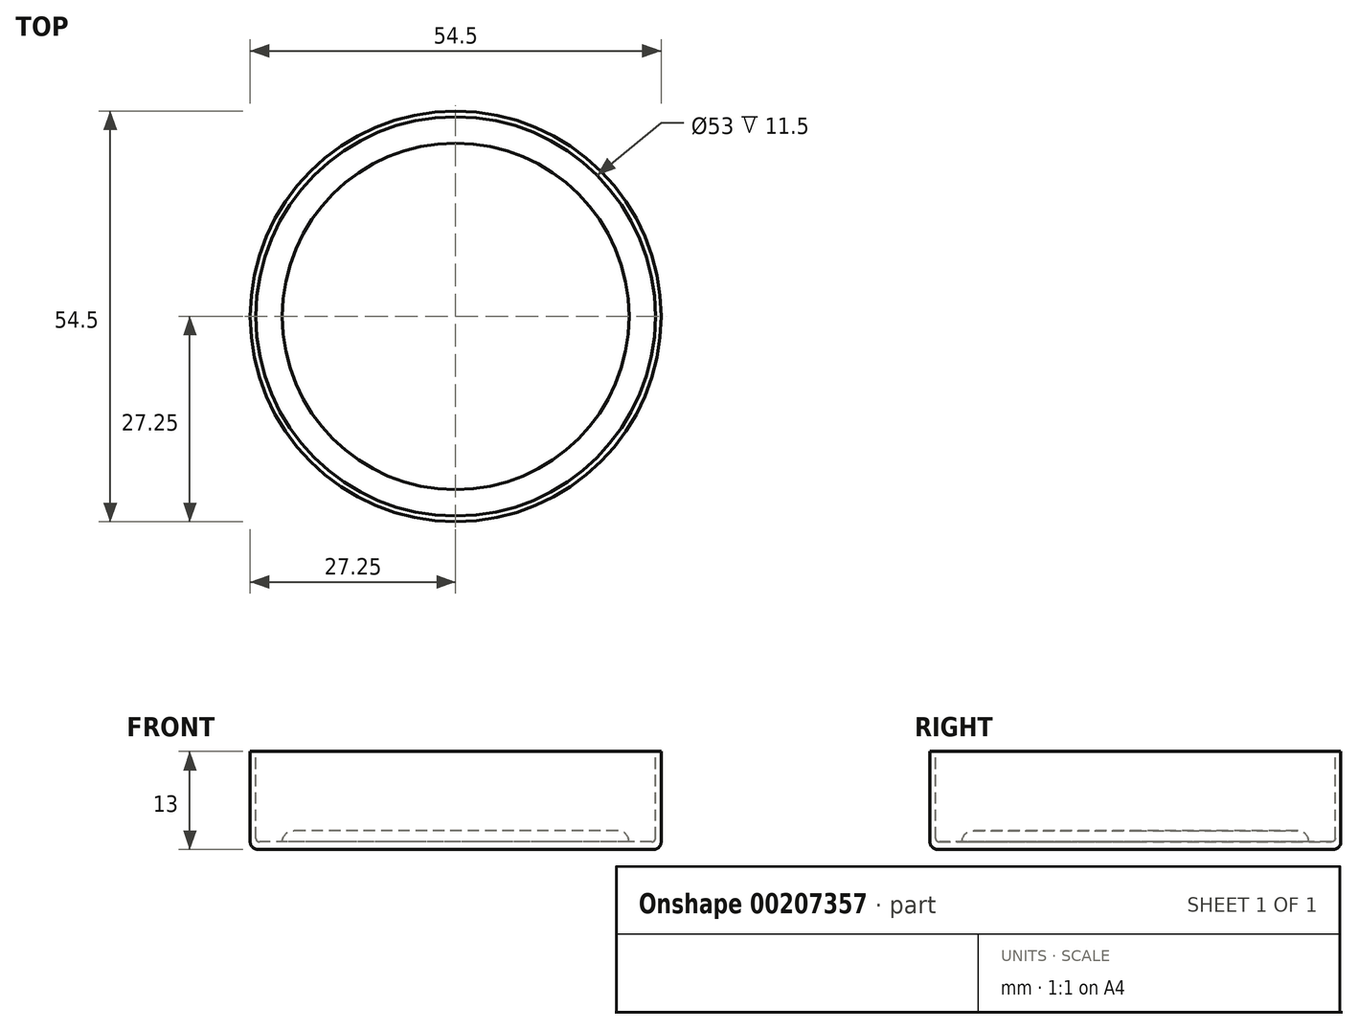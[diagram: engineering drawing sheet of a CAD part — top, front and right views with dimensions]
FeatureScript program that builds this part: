
annotation { "Feature Type Name" : "Feature", "Feature Type Description" : "" }
export const myFeature = defineFeature(function(context is Context, id is Id, definition is map)
    precondition{}
    {
        {
            var Q0;
            Q0=qCreatedBy(makeId("Top.planeOp"),FACE);
            var sketch = newSketch(context, id + "F0", { "sketchPlane" : qUnion([Q0])});
            skCircle(sketch, "E0", {"center": v(0, 0) * mm, "radius": 27.25 * mm});
            skSolve(sketch);
        }
        {
            var Q0;
            Q0=makeQuery(id+"F0.imprint","IMPRINT",FACE,{"disambiguationData":[TD([[makeQuery(id+"F0.imprint","IMPRINT",EDGE,{"derivedFrom":sQuery(id+"F0.wireOp",EDGE,"E0")}),1.0]])]});
            extrude(context, id + "F1", {"entities" : qUnion([Q0]), "depth" : 13 * mm});
        }
        {
            var Q0;
            Q0=makeQuery(id+"F1.opExtrude","CAP_FACE",FACE,{"disambiguationData":[OSD([sQuery(id+"F0.wireOp",EDGE,"E0")])],"isStart":false});
            var sketch = newSketch(context, id + "F2", { "sketchPlane" : qUnion([Q0])});
            skCircle(sketch, "E1", {"center": v(0, 0) * mm, "radius": 26.5 * mm});
            skSolve(sketch);
        }
        {
            var Q0;
            Q0=makeQuery(id+"F2.imprint","IMPRINT",FACE,{"disambiguationData":[TD([[makeQuery(id+"F2.imprint","IMPRINT",EDGE,{"derivedFrom":sQuery(id+"F2.wireOp",EDGE,"E1")}),1.0]])]});
            extrude(context, id + "F3", {"entities" : qUnion([Q0]), "operationType" : NewBodyOperationType.REMOVE, "oppositeDirection" : true, "depth" : 12 * mm});
        }
        {
            var Q0;
            Q0=makeQuery(id+"F3.boolean.opBoolean","COPY",FACE,{"derivedFrom":makeQuery(id+"F3.opExtrude","CAP_FACE",FACE,{"disambiguationData":[OSD([sQuery(id+"F2.wireOp",EDGE,"E1")])],"isStart":false})});
            var sketch = newSketch(context, id + "F4", { "sketchPlane" : qUnion([Q0])});
            skCircle(sketch, "E2", {"center": v(0, 0) * mm, "radius": 23 * mm});
            skSolve(sketch);
        }
        {
            var Q0;
            Q0=makeQuery(id+"F4.imprint","IMPRINT",FACE,{"disambiguationData":[TD([[makeQuery(id+"F4.imprint","IMPRINT",EDGE,{"derivedFrom":sQuery(id+"F4.wireOp",EDGE,"E2")}),1.0]])]});
            extrude(context, id + "F5", {"entities" : qUnion([Q0]), "operationType" : NewBodyOperationType.ADD, "depth" : 1.5 * mm});
        }
        {
            var Q0;
            Q0=makeQuery(id+"F5.opExtrude","CAP_EDGE",EDGE,{"disambiguationData":[OSD([sQuery(id+"F4.wireOp",EDGE,"E2")])],"isStart":false});
            fillet(context, id + "F6", {"entities" : qUnion([Q0]), "radius" : 1.5 * mm, "tangentPropagation" : true, "allowEdgeOverflow" : false});
        }
        {
            var Q0;
            Q0=makeQuery(id+"F1.opExtrude","CAP_FACE",FACE,{"disambiguationData":[OSD([sQuery(id+"F0.wireOp",EDGE,"E0")])],"isStart":true});
            fillet(context, id + "F7", {"entities" : qUnion([Q0]), "radius" : 1 * mm, "tangentPropagation" : true, "allowEdgeOverflow" : false});
        }
        {
            var Q0;
            Q0=makeQuery(id+"F3.boolean.opBoolean","COPY",EDGE,{"derivedFrom":makeQuery(id+"F3.opExtrude","CAP_EDGE",EDGE,{"disambiguationData":[OSD([sQuery(id+"F2.wireOp",EDGE,"E1")])],"isStart":false})});
            fillet(context, id + "F8", {"entities" : qUnion([Q0]), "radius" : 0.5 * mm, "tangentPropagation" : true, "allowEdgeOverflow" : false});
        }
    });
